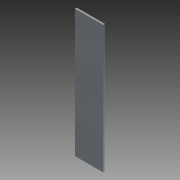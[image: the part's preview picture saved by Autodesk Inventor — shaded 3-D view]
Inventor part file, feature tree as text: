
AUTODESK INVENTOR PART (.ipt)
format: ipt  version: 2011 SP1 (Build 150282100, 282)  size: 72,704 bytes
history: native  units: in
note: dims shown in document units (in); Inventor stores cm internally (conversion verified against a paired STEP export)
features: extrude x1, sketch x1
ambient origin geometry x8: Origin, YZ Plane, XZ Plane, XY Plane, X Axis, Y Axis, Z Axis, Center Point
bodies: Solid1 (feature_tree)
feature tree (2):
  extrude  "Extrusion1"  Depth=9.0in
  sketch  "Sketch1"  dims[d0=2.0in d1=9.0in d2=4.5in d3=2.0in d4=0.125in d5=0.0in]
